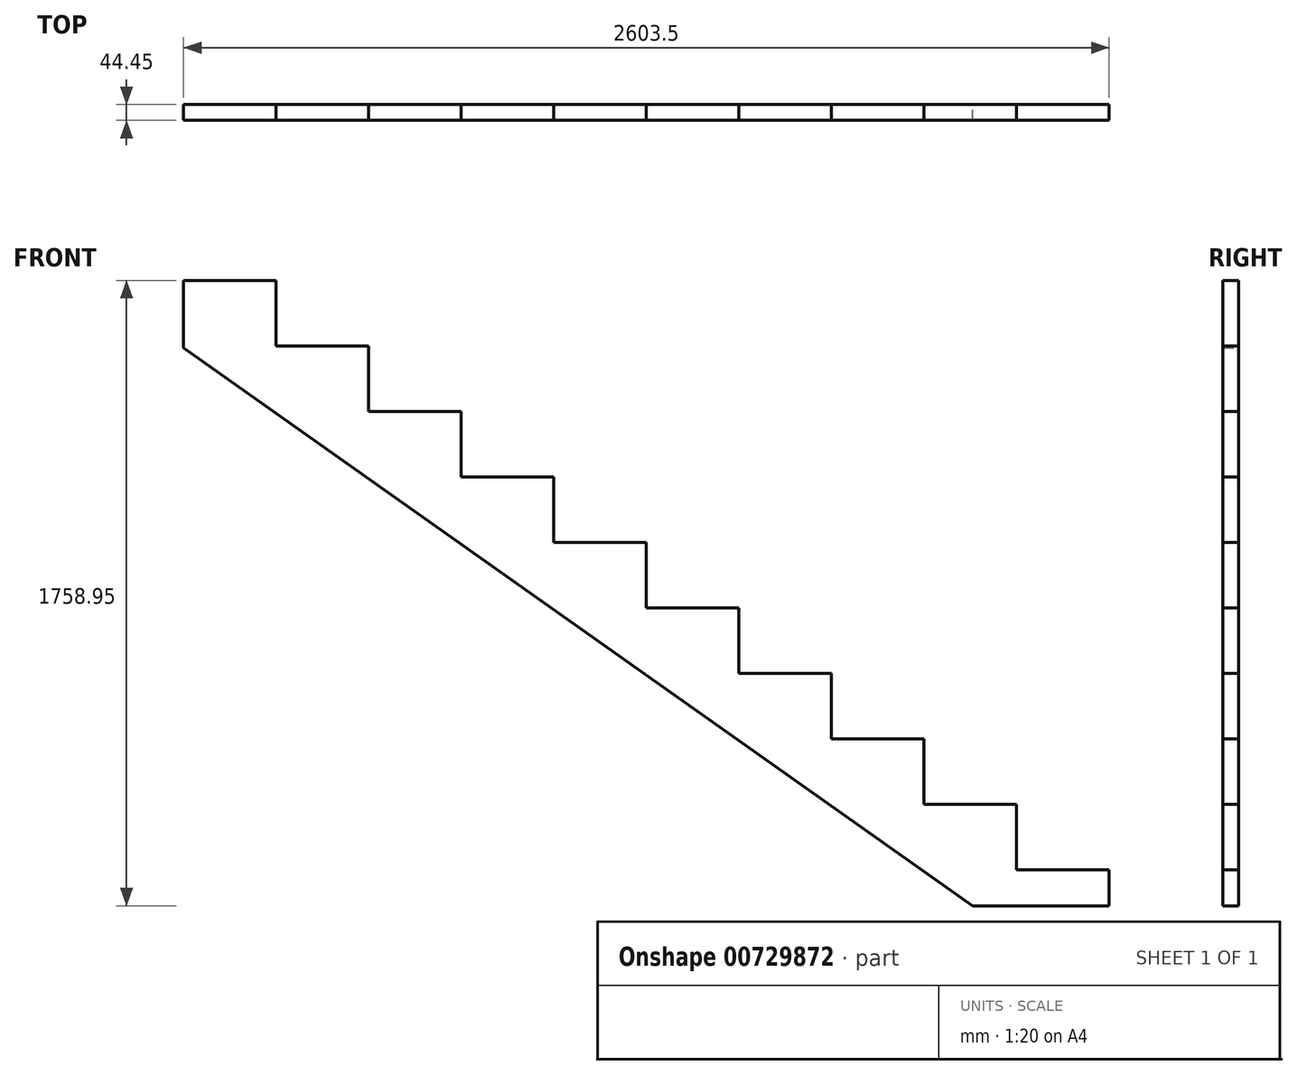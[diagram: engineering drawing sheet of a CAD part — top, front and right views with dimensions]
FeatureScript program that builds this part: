
annotation { "Feature Type Name" : "Feature", "Feature Type Description" : "" }
export const myFeature = defineFeature(function(context is Context, id is Id, definition is map)
    precondition{}
    {
        {
            var Q0;
            Q0=qCreatedBy(makeId("Front.planeOp"),FACE);
            var sketch = newSketch(context, id + "F0", { "sketchPlane" : qUnion([Q0])});
            skLineSegment(sketch, "E0", {"start": v(0, 0) * mm, "end": v(0, 101.6) * mm});
            skLineSegment(sketch, "E1", {"start": v(0, 101.6) * mm, "end": v(-260.35, 101.6) * mm});
            skLineSegment(sketch, "E2", {"start": v(-260.35, 101.6) * mm, "end": v(-260.35, 285.75) * mm});
            skLineSegment(sketch, "E3", {"start": v(0, 0) * mm, "end": v(-384.18, 0) * mm});
            skLineSegment(sketch, "E4", {"start": v(-260.35, 285.75) * mm, "end": v(-520.7, 285.75) * mm});
            skLineSegment(sketch, "E5", {"start": v(-520.7, 285.75) * mm, "end": v(-520.7, 469.9) * mm});
            skLineSegment(sketch, "E6", {"start": v(-520.7, 469.9) * mm, "end": v(-781.05, 469.9) * mm});
            skLineSegment(sketch, "E7", {"start": v(-781.05, 469.9) * mm, "end": v(-781.05, 654.05) * mm});
            skLineSegment(sketch, "E8", {"start": v(-781.05, 654.05) * mm, "end": v(-1041.4, 654.05) * mm});
            skLineSegment(sketch, "E9", {"start": v(-1041.4, 654.05) * mm, "end": v(-1041.4, 838.2) * mm});
            skLineSegment(sketch, "E10", {"start": v(-1041.4, 838.2) * mm, "end": v(-1301.75, 838.2) * mm});
            skLineSegment(sketch, "E11", {"start": v(-1301.75, 838.2) * mm, "end": v(-1301.75, 1022.35) * mm});
            skLineSegment(sketch, "E12", {"start": v(-1301.75, 1022.35) * mm, "end": v(-1562.1, 1022.35) * mm});
            skLineSegment(sketch, "E13", {"start": v(-1562.1, 1022.35) * mm, "end": v(-1562.1, 1206.5) * mm});
            skLineSegment(sketch, "E14", {"start": v(-1562.1, 1206.5) * mm, "end": v(-1822.45, 1206.5) * mm});
            skLineSegment(sketch, "E15", {"start": v(-1822.45, 1206.5) * mm, "end": v(-1822.45, 1390.65) * mm});
            skLineSegment(sketch, "E16", {"start": v(-1822.45, 1390.65) * mm, "end": v(-2082.8, 1390.65) * mm});
            skLineSegment(sketch, "E17", {"start": v(-2082.8, 1390.65) * mm, "end": v(-2082.8, 1574.8) * mm});
            skLineSegment(sketch, "E18", {"start": v(-2082.8, 1574.8) * mm, "end": v(-2343.15, 1574.8) * mm});
            skLineSegment(sketch, "E19", {"start": v(-2603.5, 1569.76) * mm, "end": v(-384.18, 0) * mm});
            skLineSegment(sketch, "E20", {"start": v(-2343.15, 1574.8) * mm, "end": v(-2343.15, 1758.95) * mm});
            skLineSegment(sketch, "E21", {"start": v(-2082.8, 1574.8) * mm, "end": v(0, 101.6) * mm, "construction": true});
            skLineSegment(sketch, "E22", {"start": v(-2343.15, 1758.95) * mm, "end": v(-2603.5, 1758.95) * mm});
            skLineSegment(sketch, "E23", {"start": v(-2603.5, 1758.95) * mm, "end": v(-2603.5, 1569.76) * mm});
            skLineSegment(sketch, "E24", {"start": v(-2603.5, 1758.95) * mm, "end": v(-2603.5, 1943.1) * mm, "construction": true});
            skSolve(sketch);
        }
        {
            var Q0;
            Q0 = qSketchRegion(id + "F0", true);
            extrude(context, id + "F1", {"entities" : qUnion([Q0]), "depth" : 44.45 * mm, "offsetDistance" : 25.4 * mm});
        }
        {
            var Q0;
            Q0=makeQuery(id+"F1.opExtrude","SWEPT_FACE",FACE,{"disambiguationData":[OSD([sQuery(id+"F0.wireOp",EDGE,"E1")])]});
            var sketch = newSketch(context, id + "F2", { "sketchPlane" : qUnion([Q0])});
            skLineSegment(sketch, "E25", {"start": v(-44.45, -44.45) * mm, "end": v(-44.45, 0) * mm, "construction": true});
            skLineSegment(sketch, "E26", {"start": v(-194.31, -44.45) * mm, "end": v(-194.31, 0) * mm, "construction": true});
            skPoint(sketch, "E27", {"position": v(-194.31, -22.23) * mm});
            skPoint(sketch, "E28", {"position": v(-44.45, -22.23) * mm});
            skSolve(sketch);
        }
        {
            var Q0;
            Q0=makeQuery(id+"F1.opExtrude","SWEPT_FACE",FACE,{"disambiguationData":[OSD([sQuery(id+"F0.wireOp",EDGE,"E22")])]});
            var sketch = newSketch(context, id + "F3", { "sketchPlane" : qUnion([Q0])});
            skLineSegment(sketch, "E29", {"start": v(-2537.46, -44.45) * mm, "end": v(-2537.46, 0) * mm, "construction": true});
            skLineSegment(sketch, "E30", {"start": v(-2387.6, -44.45) * mm, "end": v(-2387.6, 0) * mm, "construction": true});
            skPoint(sketch, "E31", {"position": v(-2537.46, -22.23) * mm});
            skPoint(sketch, "E32", {"position": v(-2387.6, -22.23) * mm});
            skSolve(sketch);
        }
        {
            var Q0;
            Q0=makeQuery(id+"F1.opExtrude","SWEPT_FACE",FACE,{"disambiguationData":[OSD([sQuery(id+"F0.wireOp",EDGE,"E18")])]});
            var sketch = newSketch(context, id + "F4", { "sketchPlane" : qUnion([Q0])});
            skLineSegment(sketch, "E33", {"start": v(-2277.11, -44.45) * mm, "end": v(-2277.11, 0) * mm, "construction": true});
            skLineSegment(sketch, "E34", {"start": v(-2127.25, -44.45) * mm, "end": v(-2127.25, 0) * mm, "construction": true});
            skPoint(sketch, "E35", {"position": v(-2277.11, -22.23) * mm});
            skPoint(sketch, "E36", {"position": v(-2127.25, -22.23) * mm});
            skSolve(sketch);
        }
        {
            var Q0;
            Q0=makeQuery(id+"F1.opExtrude","SWEPT_FACE",FACE,{"disambiguationData":[OSD([sQuery(id+"F0.wireOp",EDGE,"E20")])]});
            var sketch = newSketch(context, id + "F5", { "sketchPlane" : qUnion([Q0])});
            skLineSegment(sketch, "E37", {"start": v(-44.45, 1689.1) * mm, "end": v(0, 1689.1) * mm, "construction": true});
            skPoint(sketch, "E38", {"position": v(-22.23, 1689.1) * mm});
            skSolve(sketch);
        }
    });
